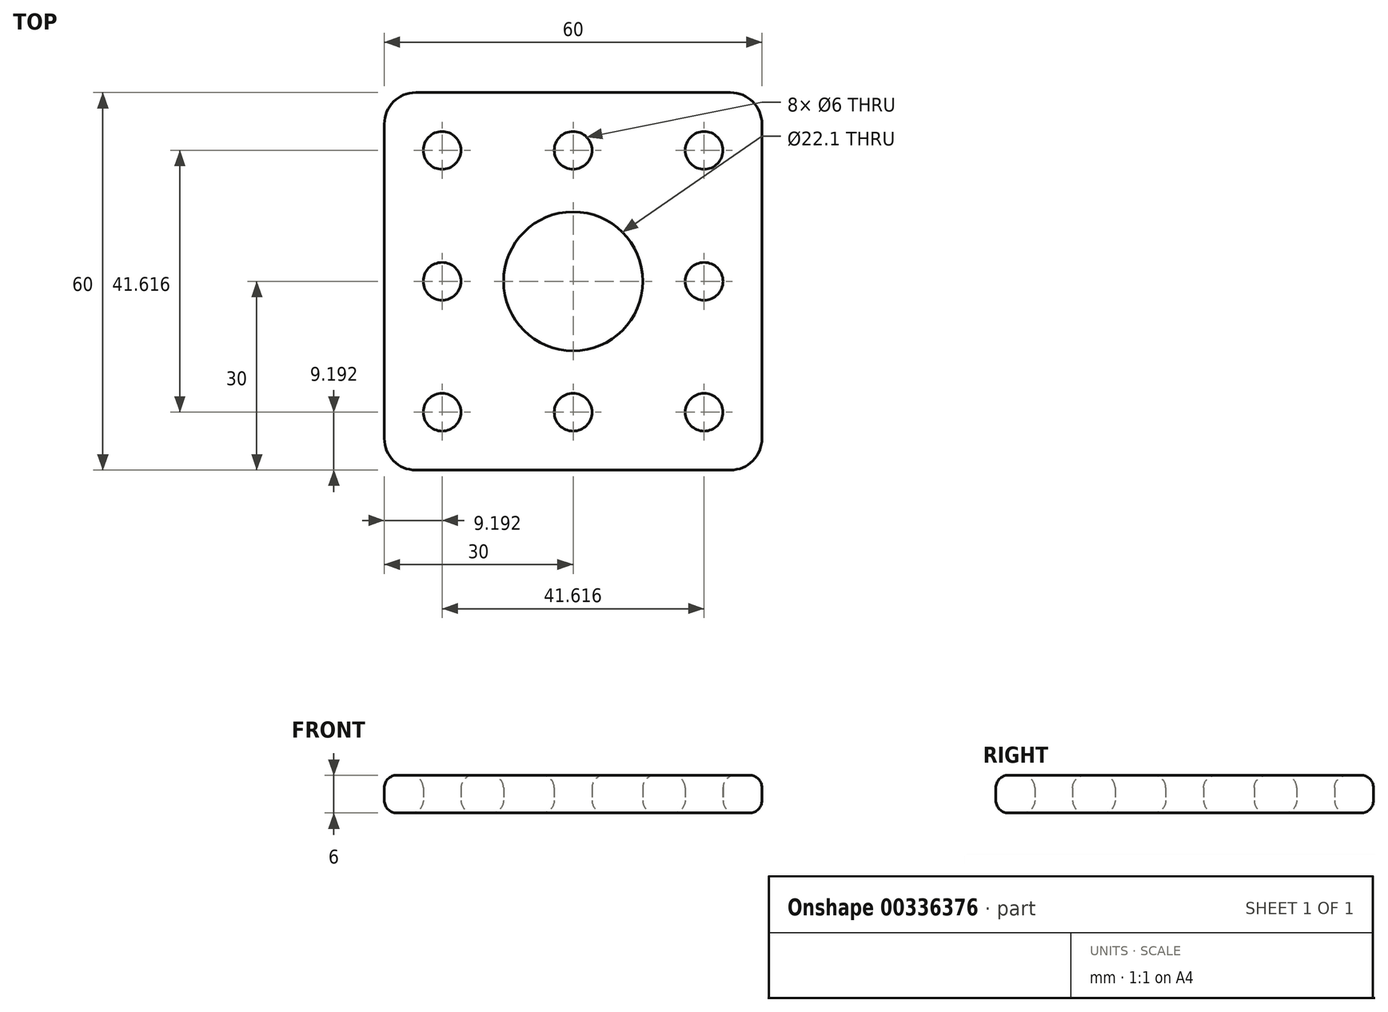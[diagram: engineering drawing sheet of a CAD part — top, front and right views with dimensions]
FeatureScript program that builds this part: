
annotation { "Feature Type Name" : "Feature", "Feature Type Description" : "" }
export const myFeature = defineFeature(function(context is Context, id is Id, definition is map)
    precondition{}
    {
        {
            var Q0;
            Q0=qCreatedBy(makeId("Top.planeOp"),FACE);
            var sketch = newSketch(context, id + "F0", { "sketchPlane" : qUnion([Q0])});
            skLineSegment(sketch, "E0.bottom", {"start": v(30, 30) * mm, "end": v(-30, 30) * mm});
            skLineSegment(sketch, "E0.top", {"start": v(30, -30) * mm, "end": v(-30, -30) * mm});
            skLineSegment(sketch, "E0.left", {"start": v(30, 30) * mm, "end": v(30, -30) * mm});
            skLineSegment(sketch, "E0.right", {"start": v(-30, 30) * mm, "end": v(-30, -30) * mm});
            skPoint(sketch, "E0.middle", {"position": v(0, 0) * mm});
            skCircle(sketch, "E1", {"center": v(0, 0) * mm, "radius": 11.05 * mm});
            skLineSegment(sketch, "E2", {"start": v(-30, 30) * mm, "end": v(0, 0) * mm});
            skCircle(sketch, "E3", {"center": v(-20.8, 20.8) * mm, "radius": 3 * mm});
            skCircle(sketch, "E4.MirrorC", {"center": v(20.8, 20.8) * mm, "radius": 3 * mm});
            skCircle(sketch, "E5.MirrorC", {"center": v(20.8, -20.8) * mm, "radius": 3 * mm});
            skCircle(sketch, "E6.MirrorC", {"center": v(-20.8, -20.8) * mm, "radius": 3 * mm});
            skCircle(sketch, "E7", {"center": v(0, 20.8) * mm, "radius": 3 * mm});
            skCircle(sketch, "E8.MirrorC", {"center": v(-20.8, 0) * mm, "radius": 3 * mm});
            skCircle(sketch, "E9.MirrorC", {"center": v(20.8, 0) * mm, "radius": 3 * mm});
            skCircle(sketch, "E10.MirrorC", {"center": v(0, -20.8) * mm, "radius": 3 * mm});
            skSolve(sketch);
        }
        {
            var Q0;
            Q0=makeQuery(id+"F0.imprint","IMPRINT",FACE,{"disambiguationData":[TD([[makeQuery(id+"F0.imprint","IMPRINT",EDGE,{"derivedFrom":sQuery(id+"F0.wireOp",EDGE,"E0.bottom")}),1.0]])]});
            extrude(context, id + "F1", {"entities" : qUnion([Q0]), "depth" : 6 * mm, "offsetDistance" : 25 * mm});
        }
        {
            var Q0;
            Q0=makeQuery(id+"F1.opExtrude","CAP_FACE",FACE,{"disambiguationData":[OSD([sQuery(id+"F0.wireOp",EDGE,"E0.bottom"),sQuery(id+"F0.wireOp",EDGE,"E0.top"),sQuery(id+"F0.wireOp",EDGE,"E0.left"),sQuery(id+"F0.wireOp",EDGE,"E0.right"),sQuery(id+"F0.wireOp",EDGE,"E1"),sQuery(id+"F0.wireOp",EDGE,"E3"),sQuery(id+"F0.wireOp",EDGE,"E4.MirrorC"),sQuery(id+"F0.wireOp",EDGE,"E5.MirrorC"),sQuery(id+"F0.wireOp",EDGE,"E6.MirrorC")])],"isStart":false});
            var Q1;
            Q1=makeQuery(id+"F1.opExtrude","CAP_FACE",FACE,{"disambiguationData":[OSD([sQuery(id+"F0.wireOp",EDGE,"E0.bottom"),sQuery(id+"F0.wireOp",EDGE,"E0.top"),sQuery(id+"F0.wireOp",EDGE,"E0.left"),sQuery(id+"F0.wireOp",EDGE,"E0.right"),sQuery(id+"F0.wireOp",EDGE,"E1"),sQuery(id+"F0.wireOp",EDGE,"E3"),sQuery(id+"F0.wireOp",EDGE,"E4.MirrorC"),sQuery(id+"F0.wireOp",EDGE,"E5.MirrorC"),sQuery(id+"F0.wireOp",EDGE,"E6.MirrorC")])],"isStart":true});
            fillet(context, id + "F2", {"entities" : qUnion([Q0, Q1]), "tangentPropagation" : true, "radius" : 2 * mm, "defaultsChanged" : true, "vertexSettings" : [], "allowEdgeOverflow" : false});
        }
        {
            var Q0;
            Q0=makeQuery(id+"F1.opExtrude","SWEPT_EDGE",EDGE,{"disambiguationData":[OSD([sQuery(id+"F0.wireOp",EDGE,"E0.top"),sQuery(id+"F0.wireOp",EDGE,"E0.right")])]});
            var Q1;
            Q1=makeQuery(id+"F1.opExtrude","SWEPT_EDGE",EDGE,{"disambiguationData":[OSD([sQuery(id+"F0.wireOp",EDGE,"E0.bottom"),sQuery(id+"F0.wireOp",EDGE,"E0.right")])]});
            var Q2;
            Q2=makeQuery(id+"F1.opExtrude","SWEPT_EDGE",EDGE,{"disambiguationData":[OSD([sQuery(id+"F0.wireOp",EDGE,"E0.bottom"),sQuery(id+"F0.wireOp",EDGE,"E0.left")])]});
            var Q3;
            Q3=makeQuery(id+"F1.opExtrude","SWEPT_EDGE",EDGE,{"disambiguationData":[OSD([sQuery(id+"F0.wireOp",EDGE,"E0.top"),sQuery(id+"F0.wireOp",EDGE,"E0.left")])]});
            fillet(context, id + "F3", {"entities" : qUnion([Q0, Q1, Q2, Q3]), "tangentPropagation" : true, "radius" : 5 * mm, "defaultsChanged" : false, "vertexSettings" : [], "allowEdgeOverflow" : false});
        }
    });
